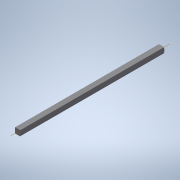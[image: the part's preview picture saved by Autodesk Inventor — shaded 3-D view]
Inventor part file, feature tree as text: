
AUTODESK INVENTOR PART (.ipt)
format: ipt  version: 2020 (Build 240168000, 168)  size: 186,880 bytes
history: native  units: in
note: dims shown in document units (in); Inventor stores cm internally (conversion verified against a paired STEP export)
features: other x5, extrude x1, plane x1, split x1, imported_body x1, sketch x1
ambient origin geometry x8: Origin, YZ Plane, XZ Plane, XY Plane, X Axis, Y Axis, Z Axis, Center Point
bodies: Body1 (feature_tree)
feature tree (10):
  parser-record x1  (decoder bookkeeping rows leaked as tree rows — omitted from the tree; the rows remain in map.json)
  other  "Shaft"
  extrude  "length cut"  Depth=4.0in
  other  "front plane"
  plane  "Work Plane3"
  split  "Split1"
  imported_body  "Base1"
  sketch  "Sketch1"  dims[d1=0.0in d2=4.0in d3=0.0in d4=0.0in d5=0.0in d6=-0.7in]
  other  "main axis"
  other  "back plane"
